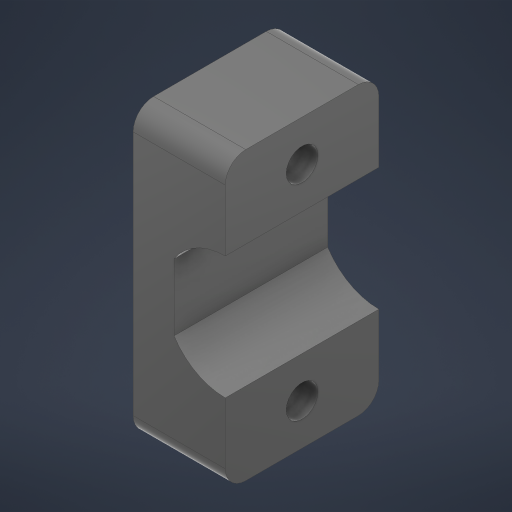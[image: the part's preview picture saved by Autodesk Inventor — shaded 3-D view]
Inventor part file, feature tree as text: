
AUTODESK INVENTOR PART (.ipt)
format: ipt  version: 2024 (Build 280153000, 153)  size: 233,984 bytes
history: native  units: in
note: dims shown in document units (in); Inventor stores cm internally (conversion verified against a paired STEP export)
features: sketch x2, extrude x1, plane x1, hole x1, fillet x1
ambient origin geometry x8: Origin, YZ Plane, XZ Plane, XY Plane, X Axis, Y Axis, Z Axis, Center Point
bodies: Body1 (feature_tree)
feature tree (6):
  extrude  "Extrusion2"  Depth=0.3543in
  plane  "Work Plane1"
  hole  "Hole1"  [1 undecoded]
  fillet  "Fillet1"  Radius=0.1575in
  sketch  "Sketch2"  dims[d8=0.5906in d9=0.0in d10=0.3543in]
  sketch  "Sketch3"  dims[d11=0.1575in d16=0.2953in d17=0.1575in d18=0.1575in d19=0.2953in d20=0.122in d21=0.2362in d22=0.1575in d23=0.0787in d24=90.0deg d25=0.315in d26=0.8108in d27=0.0787in]
note: 1 required parameter value undecoded (feature->parameter linkage not recoverable at this tier; creation-order binding heuristic only, values carry confidence <= 0.55)
